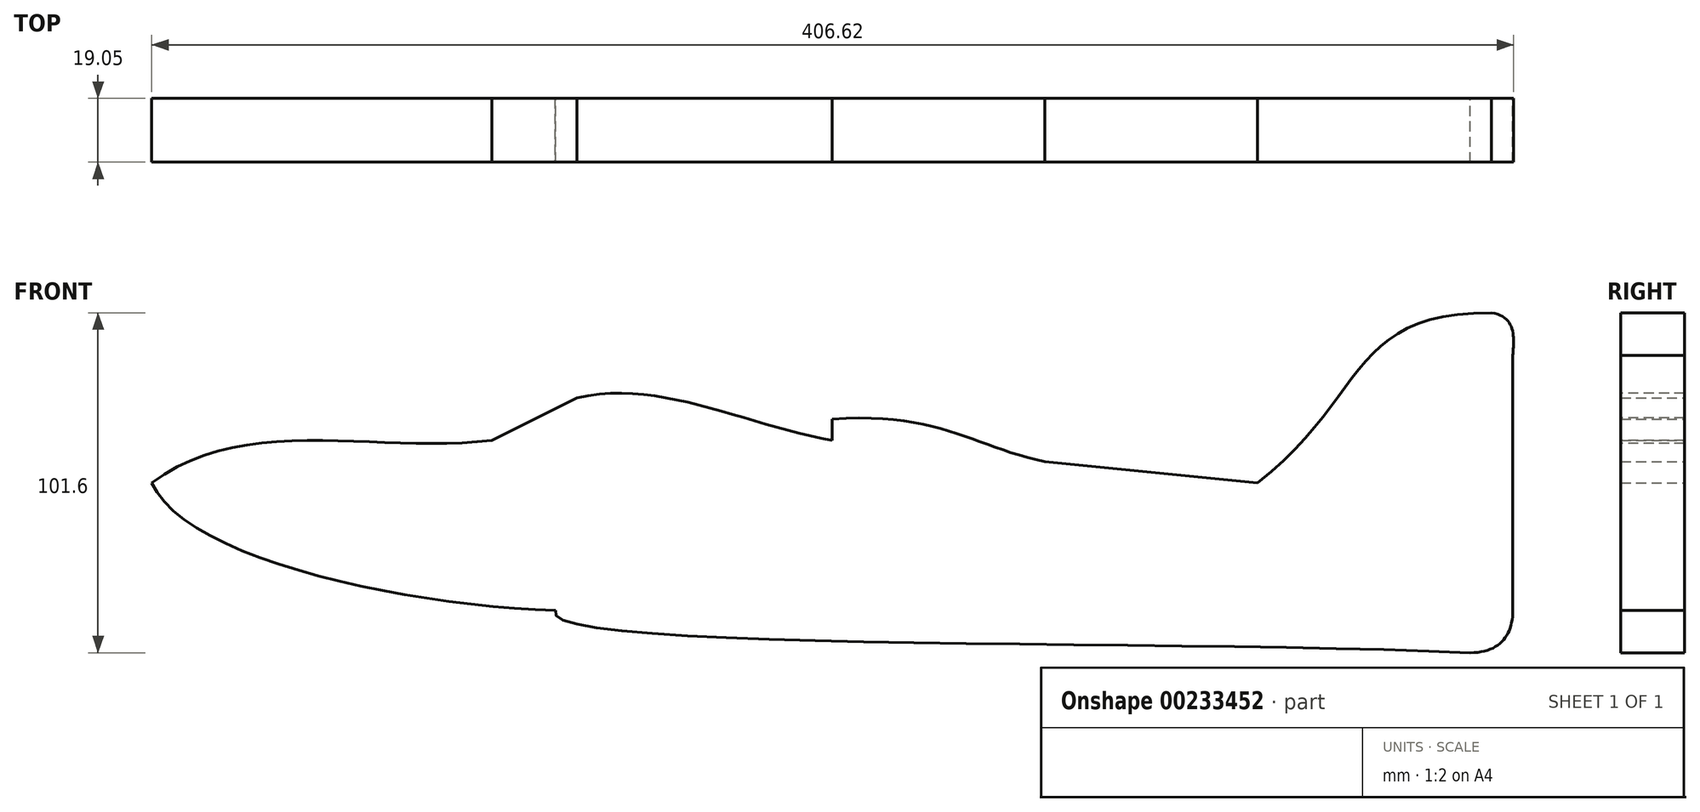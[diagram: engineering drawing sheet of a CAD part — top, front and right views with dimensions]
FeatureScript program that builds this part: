
annotation { "Feature Type Name" : "Feature", "Feature Type Description" : "" }
export const myFeature = defineFeature(function(context is Context, id is Id, definition is map)
    precondition{}
    {
        {
            var Q0;
            Q0=qCreatedBy(makeId("Front.planeOp"),FACE);
            var sketch = newSketch(context, id + "F0", { "sketchPlane" : qUnion([Q0])});
            skPoint(sketch, "E0.middle", {"position": v(0, 0) * mm});
            skFitSpline(sketch, "E1", {"points": [v(-203.2, 0) * mm, v(-101.6, 12.7) * mm], "startDerivative": vector(84.57, 63.04) * mm, "endDerivative": vector(101.6, 12.7) * mm});
            skLineSegment(sketch, "E2", {"start": v(-101.6, 12.7) * mm, "end": v(-76.2, 25.4) * mm});
            skFitSpline(sketch, "E3", {"points": [v(-76.2, 25.4) * mm, v(0, 12.7) * mm], "startDerivative": vector(76.22, 17.26) * mm, "endDerivative": vector(76.2, -12.7) * mm});
            skLineSegment(sketch, "E4", {"start": v(0, 12.7) * mm, "end": v(0, 19.05) * mm});
            skFitSpline(sketch, "E5", {"points": [v(0, 19.05) * mm, v(63.5, 6.35) * mm], "startDerivative": vector(97.2, 6.58) * mm, "endDerivative": vector(63.5, -12.7) * mm});
            skLineSegment(sketch, "E6", {"start": v(127, 0) * mm, "end": v(63.5, 6.35) * mm});
            skPoint(sketch, "E7.endSnap0", {"position": v(0, 50.8) * mm});
            skLineSegment(sketch, "E8", {"start": v(203.2, 38.1) * mm, "end": v(203.2, -38.1) * mm});
            skFitSpline(sketch, "E9", {"points": [v(190.5, -50.8) * mm, v(-82.55, -38.1) * mm], "startDerivative": vector(-273.05, 12.7) * mm, "endDerivative": vector(24.63, 38.1) * mm});
            skFitSpline(sketch, "E10", {"points": [v(196.85, 50.8) * mm, v(127, 0) * mm], "startDerivative": vector(-128.81, 0) * mm, "endDerivative": vector(-99.58, -77.95) * mm});
            skFitSpline(sketch, "E11", {"points": [v(-203.2, 0) * mm, v(-82.55, -38.1) * mm], "startDerivative": vector(28.8, -67.52) * mm, "endDerivative": vector(137.72, -3.96) * mm});
            skFitSpline(sketch, "E12", {"points": [v(203.2, 38.1) * mm, v(196.85, 50.8) * mm], "startDerivative": vector(0.84, 13.6) * mm, "endDerivative": vector(-23.18, 3.63) * mm});
            skFitSpline(sketch, "E13", {"points": [v(203.2, -38.1) * mm, v(190.5, -50.8) * mm], "startDerivative": vector(-0.26, -22.39) * mm, "endDerivative": vector(-26.86, -0.34) * mm});
            skSolve(sketch);
        }
        {
            var Q0;
            Q0 = qSketchRegion(id + "F0", true);
            extrude(context, id + "F1", {"entities" : qUnion([Q0]), "depth" : 19.05 * mm});
        }
    });
